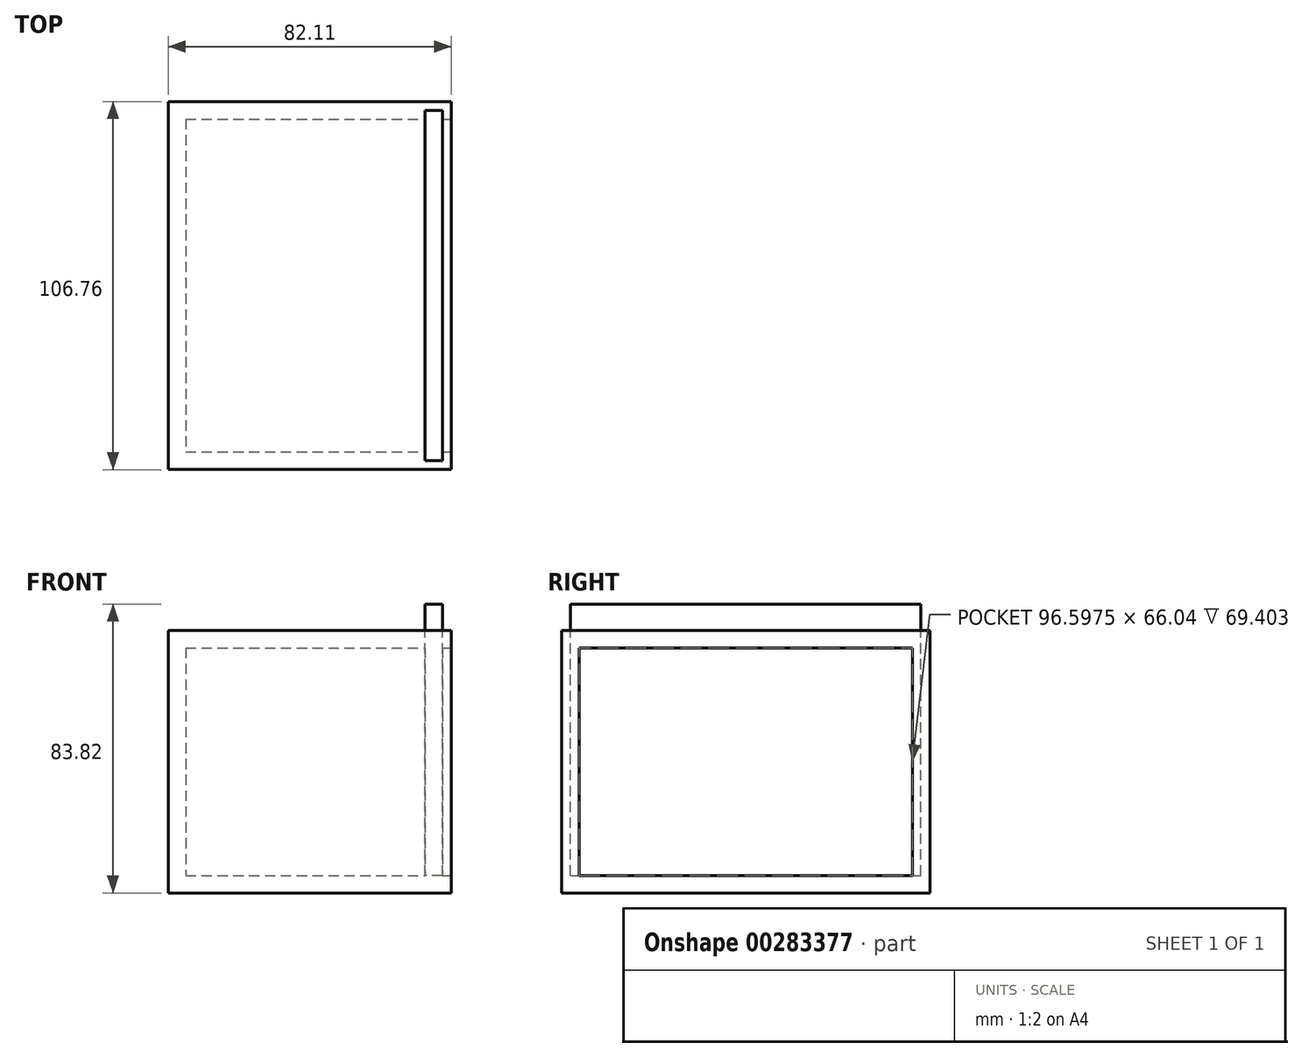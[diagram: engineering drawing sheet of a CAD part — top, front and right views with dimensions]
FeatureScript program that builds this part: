
annotation { "Feature Type Name" : "Feature", "Feature Type Description" : "" }
export const myFeature = defineFeature(function(context is Context, id is Id, definition is map)
    precondition{}
    {
        {
            var Q0;
            Q0=qCreatedBy(makeId("Top.planeOp"),FACE);
            var sketch = newSketch(context, id + "F0", { "sketchPlane" : qUnion([Q0])});
            skLineSegment(sketch, "E0.bottom", {"start": v(-33.96, 57.68) * mm, "end": v(48.15, 57.68) * mm});
            skLineSegment(sketch, "E0.top", {"start": v(-33.96, -49.08) * mm, "end": v(48.15, -49.08) * mm});
            skLineSegment(sketch, "E0.left", {"start": v(-33.96, 57.68) * mm, "end": v(-33.96, -49.08) * mm});
            skLineSegment(sketch, "E0.right", {"start": v(48.15, 57.68) * mm, "end": v(48.15, -49.08) * mm});
            skSolve(sketch);
        }
        {
            var Q0;
            Q0=makeQuery(id+"F0.imprint","IMPRINT",FACE,{"disambiguationData":[TD([[makeQuery(id+"F0.imprint","IMPRINT",EDGE,{"derivedFrom":sQuery(id+"F0.wireOp",EDGE,"E0.bottom")}),-1.0]])]});
            extrude(context, id + "F1", {"entities" : qUnion([Q0]), "depth" : 76.2 * mm});
        }
        {
            var Q0;
            Q0=makeQuery(id+"F1.opExtrude","SWEPT_FACE",FACE,{"disambiguationData":[OSD([sQuery(id+"F0.wireOp",EDGE,"E0.right")])]});
            shell(context, id + "F2", {"entities" : qUnion([Q0]), "thickness" : 5.08 * mm});
        }
        {
            var Q0;
            Q0=makeQuery(id+"F1.opExtrude","CAP_FACE",FACE,{"disambiguationData":[OSD([sQuery(id+"F0.wireOp",EDGE,"E0.bottom"),sQuery(id+"F0.wireOp",EDGE,"E0.top"),sQuery(id+"F0.wireOp",EDGE,"E0.left"),sQuery(id+"F0.wireOp",EDGE,"E0.right")])],"isStart":false});
            var sketch = newSketch(context, id + "F3", { "sketchPlane" : qUnion([Q0])});
            skLineSegment(sketch, "E1", {"start": v(48.15, -49.08) * mm, "end": v(45.6, -49.08) * mm, "construction": true});
            skLineSegment(sketch, "E2", {"start": v(45.6, -49.08) * mm, "end": v(45.6, -46.54) * mm, "construction": true});
            skLineSegment(sketch, "E3", {"start": v(45.6, -46.54) * mm, "end": v(45.6, 55.06) * mm, "construction": true});
            skLineSegment(sketch, "E4.bottom", {"start": v(45.6, -46.54) * mm, "end": v(40.53, -46.54) * mm});
            skLineSegment(sketch, "E4.top", {"start": v(45.6, 55.06) * mm, "end": v(40.53, 55.06) * mm});
            skLineSegment(sketch, "E4.left", {"start": v(45.6, -46.54) * mm, "end": v(45.6, 55.06) * mm});
            skLineSegment(sketch, "E4.right", {"start": v(40.53, -46.54) * mm, "end": v(40.53, 55.06) * mm});
            skSolve(sketch);
        }
        {
            var Q0;
            Q0=makeQuery(id+"F3.imprint","IMPRINT",FACE,{"disambiguationData":[TD([[makeQuery(id+"F3.imprint","IMPRINT",EDGE,{"derivedFrom":sQuery(id+"F3.wireOp",EDGE,"E4.bottom")}),-1.0]])]});
            extrude(context, id + "F4", {"entities" : qUnion([Q0]), "oppositeDirection" : true, "depth" : 71.12 * mm, "hasSecondDirection" : true, "secondDirectionOppositeDirection" : false, "secondDirectionDepth" : 7.62 * mm});
        }
        {
            var Q0;
            Q0=makeQuery(id+"F4.opExtrude","SWEPT_BODY",BODY,{"disambiguationData":[OSD([sQuery(id+"F3.wireOp",EDGE,"E4.bottom"),sQuery(id+"F3.wireOp",EDGE,"E4.top"),sQuery(id+"F3.wireOp",EDGE,"E4.left"),sQuery(id+"F3.wireOp",EDGE,"E4.right")])]});
            var Q1;
            Q1=makeQuery(id+"F1.opExtrude","SWEPT_BODY",BODY,{"disambiguationData":[OSD([sQuery(id+"F0.wireOp",EDGE,"E0.bottom"),sQuery(id+"F0.wireOp",EDGE,"E0.top"),sQuery(id+"F0.wireOp",EDGE,"E0.left"),sQuery(id+"F0.wireOp",EDGE,"E0.right")])]});
            booleanBodies(context, id + "F5", {"operationType" : BooleanOperationType.SUBTRACTION, "tools" : qUnion([Q0]), "targets" : qUnion([Q1]), "keepTools" : true});
        }
    });
